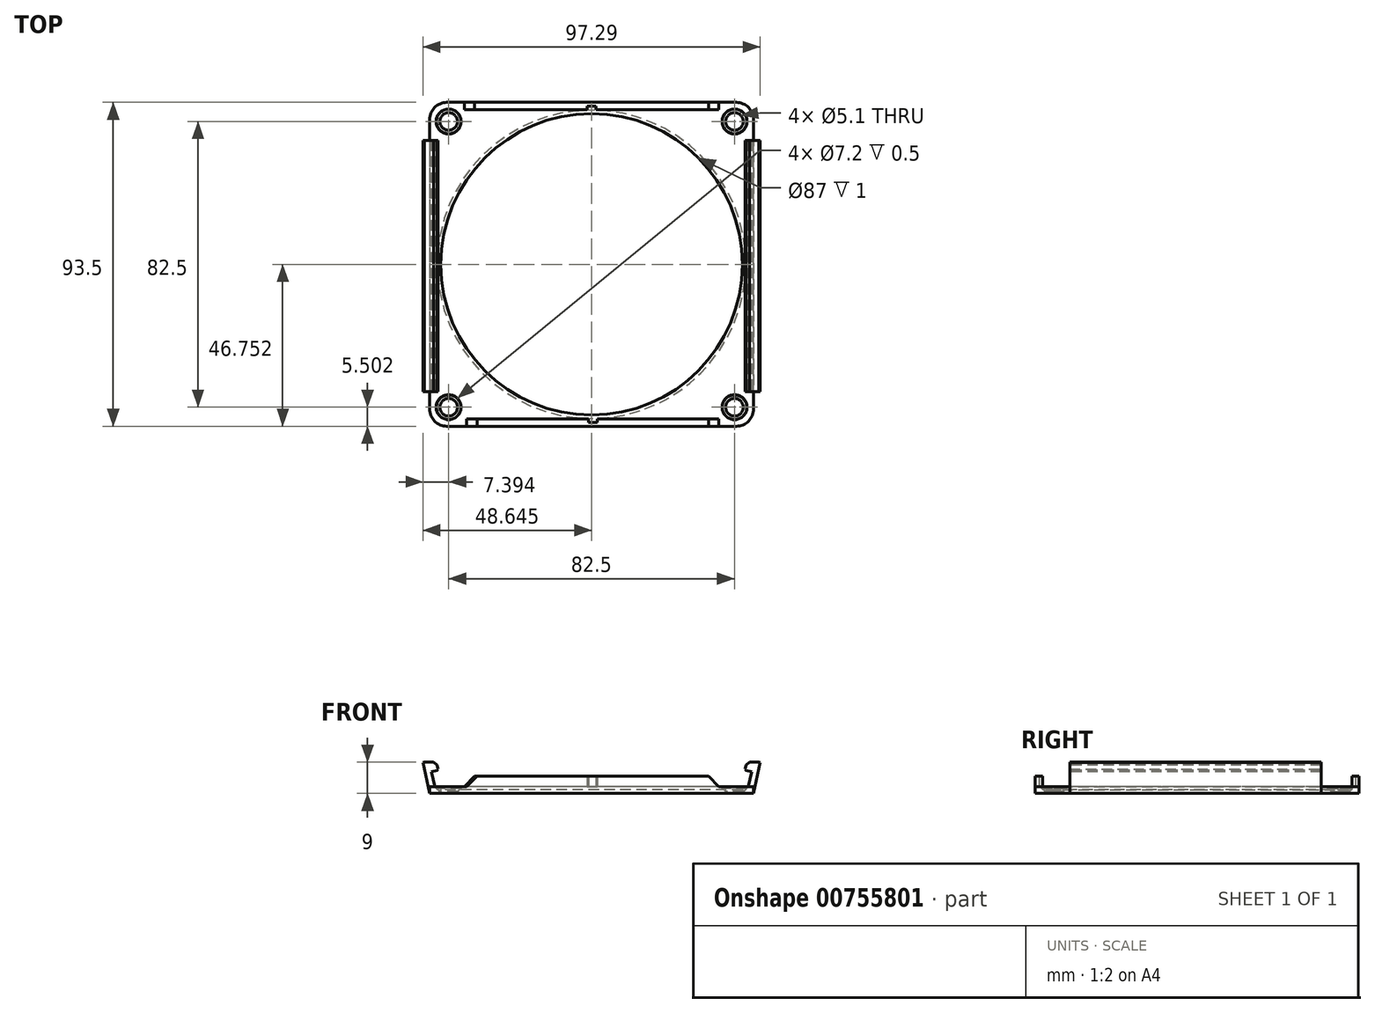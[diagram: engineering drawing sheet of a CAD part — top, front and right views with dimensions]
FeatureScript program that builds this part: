
annotation { "Feature Type Name" : "Feature", "Feature Type Description" : "" }
export const myFeature = defineFeature(function(context is Context, id is Id, definition is map)
    precondition{}
    {
        {
            var Q0;
            Q0=qCreatedBy(makeId("Top.planeOp"),FACE);
            var sketch = newSketch(context, id + "F0", { "sketchPlane" : qUnion([Q0])});
            skLineSegment(sketch, "E0.bottom", {"start": v(-16.8, 78.93) * mm, "end": v(76.7, 78.93) * mm});
            skLineSegment(sketch, "E0.top", {"start": v(-16.8, -14.57) * mm, "end": v(76.7, -14.57) * mm});
            skLineSegment(sketch, "E0.left", {"start": v(-16.8, 78.93) * mm, "end": v(-16.8, -14.57) * mm});
            skLineSegment(sketch, "E0.right", {"start": v(76.7, 78.93) * mm, "end": v(76.7, -14.57) * mm});
            skLineSegment(sketch, "E1.bottom", {"start": v(-11.3, 73.43) * mm, "end": v(71.2, 73.43) * mm, "construction": true});
            skLineSegment(sketch, "E1.top", {"start": v(-11.3, -9.07) * mm, "end": v(71.2, -9.07) * mm, "construction": true});
            skLineSegment(sketch, "E1.left", {"start": v(-11.3, 73.43) * mm, "end": v(-11.3, -9.07) * mm, "construction": true});
            skLineSegment(sketch, "E1.right", {"start": v(71.2, 73.43) * mm, "end": v(71.2, -9.07) * mm, "construction": true});
            skLineSegment(sketch, "E2", {"start": v(29.94, 73.43) * mm, "end": v(29.94, 78.93) * mm, "construction": true});
            skCircle(sketch, "E3", {"center": v(-11.3, -9.07) * mm, "radius": 2.55 * mm});
            skCircle(sketch, "E4", {"center": v(71.2, -9.07) * mm, "radius": 2.55 * mm});
            skCircle(sketch, "E5", {"center": v(-11.3, 73.43) * mm, "radius": 2.55 * mm});
            skCircle(sketch, "E6", {"center": v(71.2, 73.43) * mm, "radius": 2.55 * mm});
            skLineSegment(sketch, "E7", {"start": v(-11.3, 32.18) * mm, "end": v(-16.8, 32.18) * mm, "construction": true});
            skLineSegment(sketch, "E8", {"start": v(-11.3, 32.18) * mm, "end": v(71.2, 32.18) * mm, "construction": true});
            skCircle(sketch, "E9", {"center": v(29.94, 32.18) * mm, "radius": 43.5 * mm});
            skSolve(sketch);
        }
        {
            var Q0;
            Q0=makeQuery(id+"F0.imprint","IMPRINT",FACE,{"disambiguationData":[TD([[makeQuery(id+"F0.imprint","IMPRINT",EDGE,{"derivedFrom":sQuery(id+"F0.wireOp",EDGE,"E0.bottom")}),-1.0]])]});
            extrude(context, id + "F1", {"entities" : qUnion([Q0]), "depth" : 2 * mm, "offsetDistance" : 25 * mm});
        }
        {
            var Q0;
            Q0=makeQuery(id+"F1.opExtrude","SWEPT_FACE",FACE,{"disambiguationData":[OSD([sQuery(id+"F0.wireOp",EDGE,"E0.top")])]});
            var sketch = newSketch(context, id + "F2", { "sketchPlane" : qUnion([Q0])});
            skLineSegment(sketch, "E10", {"start": v(-15.3, 2) * mm, "end": v(-16.8, 9) * mm});
            skLineSegment(sketch, "E11", {"start": v(75.2, 2) * mm, "end": v(76.7, 9) * mm});
            skLineSegment(sketch, "E12", {"start": v(76.7, 2) * mm, "end": v(78.2, 9) * mm});
            skLineSegment(sketch, "E13", {"start": v(78.2, 9) * mm, "end": v(76.7, 9) * mm});
            skLineSegment(sketch, "E14", {"start": v(-16.8, 2) * mm, "end": v(-18.3, 9) * mm});
            skLineSegment(sketch, "E15", {"start": v(-18.3, 9) * mm, "end": v(-16.8, 9) * mm});
            skLineSegment(sketch, "E16", {"start": v(-16.8, 9) * mm, "end": v(76.7, 9) * mm, "construction": true});
            skLineSegment(sketch, "E17", {"start": v(29.94, 9) * mm, "end": v(29.94, 2) * mm, "construction": true});
            skLineSegment(sketch, "E18", {"start": v(-14.8, 9) * mm, "end": v(-16.8, 9) * mm});
            skLineSegment(sketch, "E19", {"start": v(-14.8, 9) * mm, "end": v(-14.23, 6.3) * mm, "construction": true});
            skLineSegment(sketch, "E20", {"start": v(-14.23, 6.3) * mm, "end": v(-16.23, 6.3) * mm, "construction": true});
            skLineSegment(sketch, "E21", {"start": v(-16.23, 6.3) * mm, "end": v(-14.31, 6.7) * mm});
            skLineSegment(sketch, "E22", {"start": v(-14.31, 6.7) * mm, "end": v(-14.8, 9) * mm});
            skLineSegment(sketch, "E23", {"start": v(76.7, 9) * mm, "end": v(74.7, 9) * mm});
            skLineSegment(sketch, "E24", {"start": v(74.7, 9) * mm, "end": v(74.12, 6.3) * mm});
            skLineSegment(sketch, "E25", {"start": v(74.12, 6.3) * mm, "end": v(76.12, 6.3) * mm, "construction": true});
            skLineSegment(sketch, "E26", {"start": v(76.12, 6.3) * mm, "end": v(74.2, 6.7) * mm});
            skSolve(sketch);
        }
        {
            var Q0;
            {var subQ0=sQuery(id+"F2.wireOp",EDGE,"E18");Q0=makeQuery(id+"F2.imprint","IMPRINT",FACE,{"disambiguationData":[TD([[makeQuery(id+"F2.imprint","IMPRINT",EDGE,{"derivedFrom":subQ0}),1.0]])]});}
            var Q1;
            {var subQ1=sQuery(id+"F2.wireOp",EDGE,"E14");Q1=makeQuery(id+"F2.imprint","IMPRINT",FACE,{"disambiguationData":[TD([[makeQuery(id+"F2.imprint","IMPRINT",EDGE,{"derivedFrom":subQ1}),-1.0]])]});}
            var Q2;
            {var subQ1=sQuery(id+"F2.wireOp",EDGE,"E12");Q2=makeQuery(id+"F2.imprint","IMPRINT",FACE,{"disambiguationData":[TD([[makeQuery(id+"F2.imprint","IMPRINT",EDGE,{"derivedFrom":subQ1}),1.0]])]});}
            var Q3;
            {var subQ0=sQuery(id+"F2.wireOp",EDGE,"E23");Q3=makeQuery(id+"F2.imprint","IMPRINT",FACE,{"disambiguationData":[TD([[makeQuery(id+"F2.imprint","IMPRINT",EDGE,{"derivedFrom":subQ0}),1.0]])]});}
            extrude(context, id + "F3", {"entities" : qUnion([Q0, Q1, Q2, Q3]), "operationType" : NewBodyOperationType.ADD, "oppositeDirection" : true, "depth" : (92.5 - 10) * mm, "offsetDistance" : 25 * mm, "hasSecondDirection" : true, "secondDirectionOppositeDirection" : true, "secondDirectionDepth" : 10 * mm});
        }
        {
            var Q0;
            Q0=makeQuery(id+"F3.opExtrude","SWEPT_EDGE",EDGE,{"disambiguationData":[OSD([sQuery(id+"F2.wireOp",EDGE,"E18"),sQuery(id+"F2.wireOp",EDGE,"E22")])]});
            var Q1;
            Q1=makeQuery(id+"F3.opExtrude","SWEPT_EDGE",EDGE,{"disambiguationData":[OSD([sQuery(id+"F2.wireOp",EDGE,"E23"),sQuery(id+"F2.wireOp",EDGE,"E24")])]});
            chamfer(context, id + "F4", {"entities" : qUnion([Q0, Q1]), "width" : 1 * mm, "tangentPropagation" : true});
        }
        {
            var Q0;
            Q0=makeQuery(id+"F1.opExtrude","CAP_FACE",FACE,{"disambiguationData":[OSD([sQuery(id+"F0.wireOp",EDGE,"E0.bottom"),sQuery(id+"F0.wireOp",EDGE,"E0.top"),sQuery(id+"F0.wireOp",EDGE,"E0.left"),sQuery(id+"F0.wireOp",EDGE,"E0.right"),sQuery(id+"F0.wireOp",EDGE,"E3"),sQuery(id+"F0.wireOp",EDGE,"E4"),sQuery(id+"F0.wireOp",EDGE,"E5"),sQuery(id+"F0.wireOp",EDGE,"E6")])],"isStart":false});
            var sketch = newSketch(context, id + "F5", { "sketchPlane" : qUnion([Q0])});
            skLineSegment(sketch, "E27.bottom", {"start": v(66.7, -14.57) * mm, "end": v(-6.1, -14.57) * mm});
            skLineSegment(sketch, "E27.top", {"start": v(66.7, -12.47) * mm, "end": v(-6.1, -12.47) * mm});
            skLineSegment(sketch, "E27.left", {"start": v(66.7, -14.57) * mm, "end": v(66.7, -12.47) * mm});
            skLineSegment(sketch, "E27.right", {"start": v(-6.1, -14.57) * mm, "end": v(-6.1, -12.47) * mm});
            skLineSegment(sketch, "E28.bottom", {"start": v(66.7, 78.93) * mm, "end": v(-6.8, 78.93) * mm});
            skLineSegment(sketch, "E28.top", {"start": v(66.7, 76.83) * mm, "end": v(-6.8, 76.83) * mm});
            skLineSegment(sketch, "E28.left", {"start": v(66.7, 78.93) * mm, "end": v(66.7, 76.83) * mm});
            skLineSegment(sketch, "E28.right", {"start": v(-6.8, 78.93) * mm, "end": v(-6.8, 76.83) * mm});
            skLineSegment(sketch, "E29", {"start": v(29.05, -13.47) * mm, "end": v(31.55, -13.47) * mm});
            skLineSegment(sketch, "E30", {"start": v(30.3, -13.47) * mm, "end": v(30.3, -12.47) * mm, "construction": true});
            skLineSegment(sketch, "E31", {"start": v(31.55, -13.47) * mm, "end": v(31.55, -12.47) * mm});
            skLineSegment(sketch, "E32", {"start": v(29.05, -13.47) * mm, "end": v(29.05, -12.47) * mm});
            skLineSegment(sketch, "E33", {"start": v(28.7, 77.83) * mm, "end": v(31.2, 77.83) * mm});
            skLineSegment(sketch, "E34", {"start": v(29.94, 77.83) * mm, "end": v(29.94, 76.83) * mm, "construction": true});
            skLineSegment(sketch, "E35", {"start": v(28.7, 77.83) * mm, "end": v(28.7, 76.83) * mm});
            skLineSegment(sketch, "E36", {"start": v(31.2, 77.83) * mm, "end": v(31.2, 76.83) * mm});
            skSolve(sketch);
        }
        {
            var Q0;
            Q0=makeQuery(id+"F5.imprint","IMPRINT",FACE,{"disambiguationData":[TD([[makeQuery(id+"F5.imprint","IMPRINT",EDGE,{"derivedFrom":sQuery(id+"F5.wireOp",EDGE,"E27.bottom")}),1.0]])]});
            var Q1;
            Q1=makeQuery(id+"F5.imprint","IMPRINT",FACE,{"disambiguationData":[TD([[makeQuery(id+"F5.imprint","IMPRINT",EDGE,{"derivedFrom":sQuery(id+"F5.wireOp",EDGE,"E28.bottom")}),-1.0]])]});
            extrude(context, id + "F6", {"entities" : qUnion([Q0, Q1]), "operationType" : NewBodyOperationType.ADD, "depth" : 3 * mm, "offsetDistance" : 25 * mm});
        }
        {
            var Q0;
            Q0=makeQuery(id+"F6.opExtrude","CAP_EDGE",EDGE,{"disambiguationData":[OSD([sQuery(id+"F5.wireOp",EDGE,"E27.left")])],"isStart":false});
            var Q1;
            Q1=makeQuery(id+"F6.opExtrude","CAP_EDGE",EDGE,{"disambiguationData":[OSD([sQuery(id+"F5.wireOp",EDGE,"E27.right")])],"isStart":false});
            var Q2;
            Q2=makeQuery(id+"F6.opExtrude","CAP_EDGE",EDGE,{"disambiguationData":[OSD([sQuery(id+"F5.wireOp",EDGE,"E28.right")])],"isStart":false});
            var Q3;
            Q3=makeQuery(id+"F6.opExtrude","CAP_EDGE",EDGE,{"disambiguationData":[OSD([sQuery(id+"F5.wireOp",EDGE,"E28.left")])],"isStart":false});
            chamfer(context, id + "F7", {"entities" : qUnion([Q0, Q1, Q2, Q3]), "width" : 3 * mm, "tangentPropagation" : true});
        }
        {
            var Q0;
            Q0=makeQuery(id+"F1.opExtrude","CAP_FACE",FACE,{"disambiguationData":[OSD([sQuery(id+"F0.wireOp",EDGE,"E0.bottom"),sQuery(id+"F0.wireOp",EDGE,"E0.top"),sQuery(id+"F0.wireOp",EDGE,"E0.left"),sQuery(id+"F0.wireOp",EDGE,"E0.right"),sQuery(id+"F0.wireOp",EDGE,"E3"),sQuery(id+"F0.wireOp",EDGE,"E4"),sQuery(id+"F0.wireOp",EDGE,"E5"),sQuery(id+"F0.wireOp",EDGE,"E6"),sQuery(id+"F0.wireOp",EDGE,"E9")])],"isStart":false});
            var sketch = newSketch(context, id + "F8", { "sketchPlane" : qUnion([Q0])});
            skCircle(sketch, "E37", {"center": v(-11.3, -9.07) * mm, "radius": 3.6 * mm});
            skCircle(sketch, "E38", {"center": v(71.2, -9.07) * mm, "radius": 3.6 * mm});
            skCircle(sketch, "E39", {"center": v(71.2, 73.43) * mm, "radius": 3.6 * mm});
            skCircle(sketch, "E40", {"center": v(-11.3, 73.43) * mm, "radius": 3.6 * mm});
            skSolve(sketch);
        }
        {
            var Q0;
            Q0=qSketchRegion(id+"F8",true);
            extrude(context, id + "F9", {"entities" : qUnion([Q0]), "operationType" : NewBodyOperationType.REMOVE, "oppositeDirection" : true, "depth" : .5 * mm, "offsetDistance" : 25 * mm});
        }
        {
            var Q0;
            Q0=makeQuery(id+"F9.boolean.opBoolean","INTERSECT",EDGE,{"derivedFrom":[makeQuery(id+"F1.opExtrude","SWEPT_FACE",FACE,{"disambiguationData":[OSD([sQuery(id+"F0.wireOp",EDGE,"E3")])]}),makeQuery(id+"F9.opExtrude","CAP_FACE",FACE,{"disambiguationData":[OSD([sQuery(id+"F8.wireOp",EDGE,"E37")])],"isStart":false})]});
            var Q1;
            Q1=makeQuery(id+"F9.boolean.opBoolean","INTERSECT",EDGE,{"derivedFrom":[makeQuery(id+"F1.opExtrude","SWEPT_FACE",FACE,{"disambiguationData":[OSD([sQuery(id+"F0.wireOp",EDGE,"E4")])]}),makeQuery(id+"F9.opExtrude","CAP_FACE",FACE,{"disambiguationData":[OSD([sQuery(id+"F8.wireOp",EDGE,"E38")])],"isStart":false})]});
            var Q2;
            Q2=makeQuery(id+"F9.boolean.opBoolean","INTERSECT",EDGE,{"derivedFrom":[makeQuery(id+"F1.opExtrude","SWEPT_FACE",FACE,{"disambiguationData":[OSD([sQuery(id+"F0.wireOp",EDGE,"E6")])]}),makeQuery(id+"F9.opExtrude","CAP_FACE",FACE,{"disambiguationData":[OSD([sQuery(id+"F8.wireOp",EDGE,"E39")])],"isStart":false})]});
            var Q3;
            Q3=makeQuery(id+"F9.boolean.opBoolean","INTERSECT",EDGE,{"derivedFrom":[makeQuery(id+"F1.opExtrude","SWEPT_FACE",FACE,{"disambiguationData":[OSD([sQuery(id+"F0.wireOp",EDGE,"E5")])]}),makeQuery(id+"F9.opExtrude","CAP_FACE",FACE,{"disambiguationData":[OSD([sQuery(id+"F8.wireOp",EDGE,"E40")])],"isStart":false})]});
            chamfer(context, id + "F10", {"entities" : qUnion([Q0, Q1, Q2, Q3]), "width" : 1 * mm, "tangentPropagation" : true});
        }
        {
            var Q0;
            Q0=makeQuery(id+"F1.opExtrude","SWEPT_EDGE",EDGE,{"disambiguationData":[OSD([sQuery(id+"F0.wireOp",EDGE,"E0.bottom"),sQuery(id+"F0.wireOp",EDGE,"E0.left")])]});
            var Q1;
            Q1=makeQuery(id+"F1.opExtrude","SWEPT_EDGE",EDGE,{"disambiguationData":[OSD([sQuery(id+"F0.wireOp",EDGE,"E0.top"),sQuery(id+"F0.wireOp",EDGE,"E0.left")])]});
            var Q2;
            Q2=makeQuery(id+"F1.opExtrude","SWEPT_EDGE",EDGE,{"disambiguationData":[OSD([sQuery(id+"F0.wireOp",EDGE,"E0.top"),sQuery(id+"F0.wireOp",EDGE,"E0.right")])]});
            var Q3;
            Q3=makeQuery(id+"F1.opExtrude","SWEPT_EDGE",EDGE,{"disambiguationData":[OSD([sQuery(id+"F0.wireOp",EDGE,"E0.bottom"),sQuery(id+"F0.wireOp",EDGE,"E0.right")])]});
            fillet(context, id + "F11", {"entities" : qUnion([Q0, Q1, Q2, Q3]), "radius" : 5 * mm, "tangentPropagation" : true, "allowEdgeOverflow" : false});
        }
        {
            var Q0;
            Q0=makeQuery(id+"F1.opExtrude","CAP_EDGE",EDGE,{"disambiguationData":[OSD([sQuery(id+"F0.wireOp",EDGE,"E9")])],"isStart":true});
            chamfer(context, id + "F12", {"entities" : qUnion([Q0]), "width" : 1 * mm, "tangentPropagation" : true});
        }
        {
            var Q0;
            Q0=makeQuery(id+"F3.opExtrude","SWEPT_EDGE",EDGE,{"disambiguationData":[OSD([sQuery(id+"F2.wireOp",EDGE,"E21"),sQuery(id+"F2.wireOp",EDGE,"E22")])]});
            var Q1;
            Q1=makeQuery(id+"F3.opExtrude","SWEPT_EDGE",EDGE,{"disambiguationData":[OSD([sQuery(id+"F2.wireOp",EDGE,"E24"),sQuery(id+"F2.wireOp",EDGE,"E26")])]});
            chamfer(context, id + "F13", {"entities" : qUnion([Q0, Q1]), "width" : .3 * mm, "tangentPropagation" : true});
        }
        {
            var Q0;
            Q0=makeQuery(id+"F3.opExtrude","SWEPT_FACE",FACE,{"disambiguationData":[OSD([sQuery(id+"F2.wireOp",EDGE,"E14")])]});
            extrude(context, id + "F14", {"entities" : qUnion([Q0]), "operationType" : NewBodyOperationType.ADD, "depth" : .4 * mm, "offsetDistance" : 25 * mm});
        }
        {
            var Q0;
            Q0=makeQuery(id+"F3.opExtrude","SWEPT_FACE",FACE,{"disambiguationData":[OSD([sQuery(id+"F2.wireOp",EDGE,"E12")])]});
            extrude(context, id + "F15", {"entities" : qUnion([Q0]), "operationType" : NewBodyOperationType.ADD, "depth" : .4 * mm, "offsetDistance" : 25 * mm});
        }
        {
            var Q0;
            Q0=makeQuery(id+"F15.opExtrude","SWEPT_FACE",FACE,{"disambiguationData":[OSD([sQuery(id+"F0.wireOp",EDGE,"E0.top"),sQuery(id+"F0.wireOp",EDGE,"E0.right"),sQuery(id+"F2.wireOp",EDGE,"E12")])]});
            var Q1;
            Q1=makeQuery(id+"F1.opExtrude","SWEPT_FACE",FACE,{"disambiguationData":[OSD([sQuery(id+"F0.wireOp",EDGE,"E0.right")])]});
            extrude(context, id + "F16", {"entities" : qUnion([Q0]), "operationType" : NewBodyOperationType.ADD, "endBound" : BoundingType.UP_TO_SURFACE, "depth" : 25 * mm, "endBoundEntityFace" : qUnion([Q1]), "offsetDistance" : 25 * mm});
        }
        {
            var Q0;
            Q0=makeQuery(id+"F14.opExtrude","SWEPT_FACE",FACE,{"disambiguationData":[OSD([sQuery(id+"F0.wireOp",EDGE,"E0.top"),sQuery(id+"F0.wireOp",EDGE,"E0.left"),sQuery(id+"F2.wireOp",EDGE,"E14")])]});
            var Q1;
            Q1=makeQuery(id+"F1.opExtrude","SWEPT_FACE",FACE,{"disambiguationData":[OSD([sQuery(id+"F0.wireOp",EDGE,"E0.left")])]});
            extrude(context, id + "F17", {"entities" : qUnion([Q0]), "operationType" : NewBodyOperationType.ADD, "endBound" : BoundingType.UP_TO_SURFACE, "depth" : 25 * mm, "endBoundEntityFace" : qUnion([Q1]), "offsetDistance" : 25 * mm});
        }
    });
